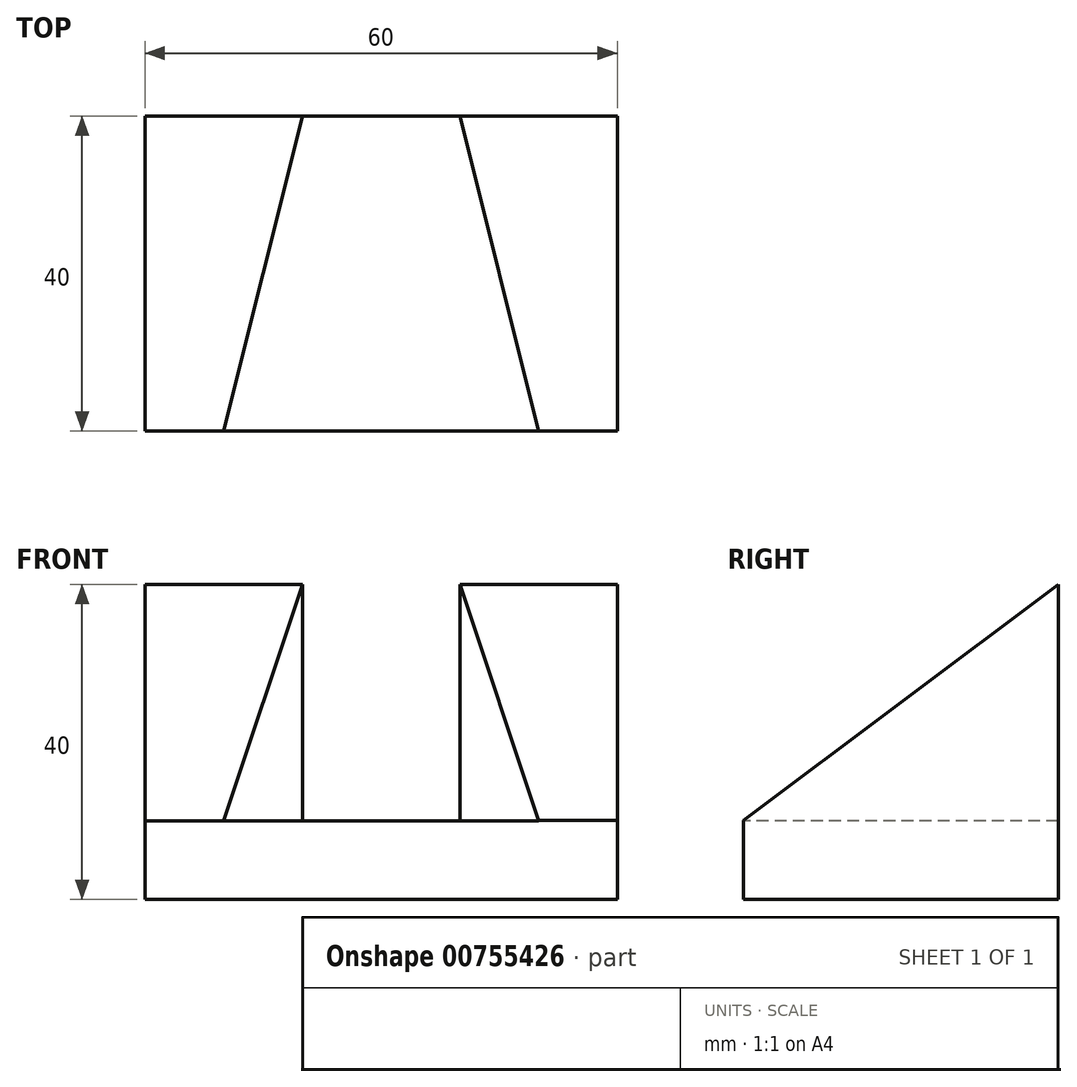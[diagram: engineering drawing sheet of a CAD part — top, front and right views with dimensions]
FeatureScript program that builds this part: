
annotation { "Feature Type Name" : "Feature", "Feature Type Description" : "" }
export const myFeature = defineFeature(function(context is Context, id is Id, definition is map)
    precondition{}
    {
        {
            var Q0;
            Q0=qCreatedBy(makeId("Front.planeOp"),FACE);
            var sketch = newSketch(context, id + "F0", { "sketchPlane" : qUnion([Q0])});
            skLineSegment(sketch, "E0", {"start": v(0, 0) * mm, "end": v(60, 0) * mm});
            skLineSegment(sketch, "E1", {"start": v(60, 0) * mm, "end": v(60, 40) * mm});
            skLineSegment(sketch, "E2", {"start": v(60, 40) * mm, "end": v(0, 40) * mm});
            skLineSegment(sketch, "E3", {"start": v(0, 40) * mm, "end": v(0, 0) * mm});
            skSolve(sketch);
        }
        {
            var Q0;
            Q0=makeQuery(id+"F0.imprint","IMPRINT",FACE,{"disambiguationData":[TD([[makeQuery(id+"F0.imprint","IMPRINT",EDGE,{"derivedFrom":sQuery(id+"F0.wireOp",EDGE,"E0")}),1.0]])]});
            extrude(context, id + "F1", {"entities" : qUnion([Q0]), "depth" : 40 * mm, "offsetDistance" : 25 * mm});
        }
        {
            var Q0;
            Q0=makeQuery(id+"F1.opExtrude","SWEPT_FACE",FACE,{"disambiguationData":[OSD([sQuery(id+"F0.wireOp",EDGE,"E2")])]});
            var sketch = newSketch(context, id + "F2", { "sketchPlane" : qUnion([Q0])});
            skLineSegment(sketch, "E4", {"start": v(20, 0) * mm, "end": v(40, 0) * mm});
            skLineSegment(sketch, "E5", {"start": v(10, -40) * mm, "end": v(50, -40) * mm});
            skLineSegment(sketch, "E6", {"start": v(20, 0) * mm, "end": v(10, -40) * mm});
            skLineSegment(sketch, "E7", {"start": v(40, 0) * mm, "end": v(50, -40) * mm});
            skSolve(sketch);
        }
        {
            var Q0;
            Q0=makeQuery(id+"F2.imprint","IMPRINT",FACE,{"disambiguationData":[TD([[makeQuery(id+"F2.imprint","IMPRINT",EDGE,{"derivedFrom":sQuery(id+"F2.wireOp",EDGE,"E4")}),1.0]])]});
            extrude(context, id + "F3", {"entities" : qUnion([Q0]), "operationType" : NewBodyOperationType.REMOVE, "oppositeDirection" : true, "depth" : 30 * mm, "offsetDistance" : 25 * mm});
        }
        {
            var Q0;
            Q0=makeQuery(id+"F1.opExtrude","CAP_FACE",FACE,{"disambiguationData":[OSD([sQuery(id+"F0.wireOp",EDGE,"E0"),sQuery(id+"F0.wireOp",EDGE,"E1"),sQuery(id+"F0.wireOp",EDGE,"E2"),sQuery(id+"F0.wireOp",EDGE,"E3")])],"isStart":false});
            var sketch = newSketch(context, id + "F4", { "sketchPlane" : qUnion([Q0])});
            skLineSegment(sketch, "E8", {"start": v(10, 10) * mm, "end": v(0, 10) * mm});
            skSolve(sketch);
        }
        {
            var Q0;
            Q0=makeQuery(id+"F1.opExtrude","SWEPT_FACE",FACE,{"disambiguationData":[OSD([sQuery(id+"F0.wireOp",EDGE,"E3")])]});
            var sketch = newSketch(context, id + "F5", { "sketchPlane" : qUnion([Q0])});
            skLineSegment(sketch, "E9", {"start": v(0, 40) * mm, "end": v(40, 10) * mm});
            skSolve(sketch);
        }
        {
            var Q0;
            {var subQ0=sQuery(id+"F5.wireOp",EDGE,"E9");Q0=makeQuery(id+"F5.imprint","IMPRINT",FACE,{"disambiguationData":[TD([[makeQuery(id+"F5.imprint","IMPRINT",EDGE,{"derivedFrom":subQ0}),1.0]])]});}
            extrude(context, id + "F6", {"entities" : qUnion([Q0]), "operationType" : NewBodyOperationType.REMOVE, "oppositeDirection" : true, "depth" : 25 * mm, "offsetDistance" : 25 * mm});
        }
        {
            var Q0;
            {var subQ0=sQuery(id+"F4.wireOp",EDGE,"E8");Q0=makeQuery(id+"F4.imprint","IMPRINT",FACE,{"disambiguationData":[TD([[makeQuery(id+"F4.imprint","IMPRINT",EDGE,{"derivedFrom":subQ0}),-1.0]])]});}
            extrude(context, id + "F7", {"entities" : qUnion([Q0]), "operationType" : NewBodyOperationType.REMOVE, "depth" : 25 * mm, "offsetDistance" : 25 * mm});
        }
        {
            var Q0;
            Q0=makeQuery(id+"F1.opExtrude","CAP_FACE",FACE,{"disambiguationData":[OSD([sQuery(id+"F0.wireOp",EDGE,"E0"),sQuery(id+"F0.wireOp",EDGE,"E1"),sQuery(id+"F0.wireOp",EDGE,"E2"),sQuery(id+"F0.wireOp",EDGE,"E3")])],"isStart":false});
            var sketch = newSketch(context, id + "F8", { "sketchPlane" : qUnion([Q0])});
            skLineSegment(sketch, "E10", {"start": v(50, 10) * mm, "end": v(60, 10) * mm});
            skSolve(sketch);
        }
        {
            var Q0;
            Q0=makeQuery(id+"F1.opExtrude","SWEPT_FACE",FACE,{"disambiguationData":[OSD([sQuery(id+"F0.wireOp",EDGE,"E1")])]});
            var sketch = newSketch(context, id + "F9", { "sketchPlane" : qUnion([Q0])});
            skLineSegment(sketch, "E11", {"start": v(0, 40) * mm, "end": v(-40, 10) * mm});
            skSolve(sketch);
        }
        {
            var Q0;
            {var subQ0=sQuery(id+"F9.wireOp",EDGE,"E11");Q0=makeQuery(id+"F9.imprint","IMPRINT",FACE,{"disambiguationData":[TD([[makeQuery(id+"F9.imprint","IMPRINT",EDGE,{"derivedFrom":subQ0}),-1.0]])]});}
            extrude(context, id + "F10", {"entities" : qUnion([Q0]), "operationType" : NewBodyOperationType.REMOVE, "oppositeDirection" : true, "depth" : 25 * mm, "offsetDistance" : 25 * mm});
        }
        {
            var Q0;
            {var subQ0=sQuery(id+"F8.wireOp",EDGE,"E10");Q0=makeQuery(id+"F8.imprint","IMPRINT",FACE,{"disambiguationData":[TD([[makeQuery(id+"F8.imprint","IMPRINT",EDGE,{"derivedFrom":subQ0}),1.0]])]});}
            extrude(context, id + "F11", {"entities" : qUnion([Q0]), "operationType" : NewBodyOperationType.REMOVE, "depth" : 25 * mm, "offsetDistance" : 25 * mm});
        }
    });
